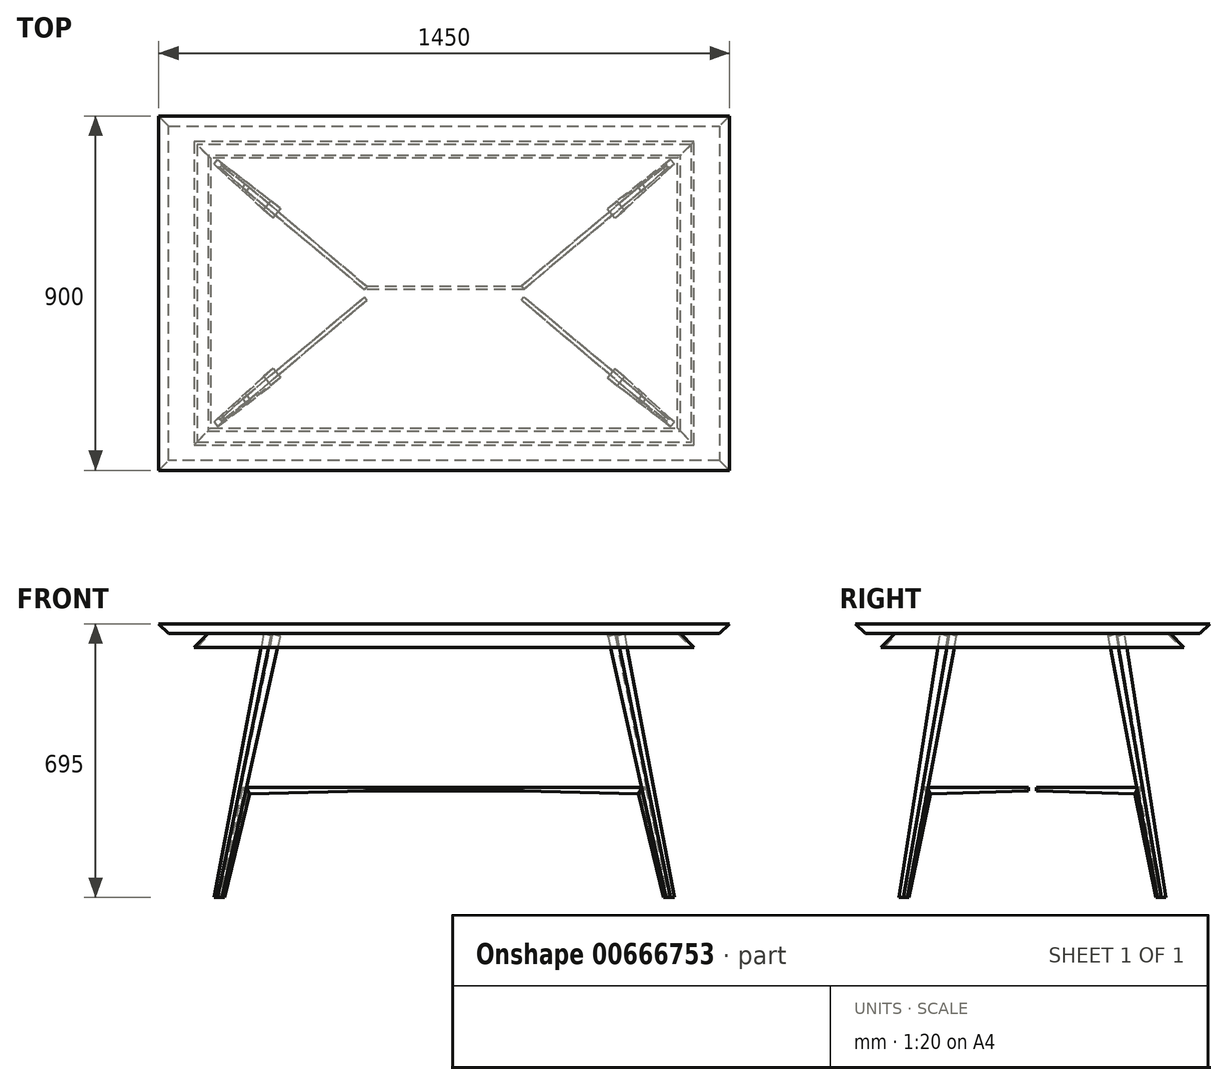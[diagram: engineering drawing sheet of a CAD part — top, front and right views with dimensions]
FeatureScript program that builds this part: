
annotation { "Feature Type Name" : "Feature", "Feature Type Description" : "" }
export const myFeature = defineFeature(function(context is Context, id is Id, definition is map)
    precondition{}
    {
        {
            assignVariable(context, id + "F0", {"name" : "t_l", "anyValue" : 30});
        }
        {
            var Q0;
            Q0=qCreatedBy(makeId("Top.planeOp"),FACE);
            var sketch = newSketch(context, id + "F1", { "sketchPlane" : qUnion([Q0])});
            skLineSegment(sketch, "E0.bottom", {"start": v(600, -350) * mm, "end": v(-600, -350) * mm});
            skLineSegment(sketch, "E0.top", {"start": v(600, 350) * mm, "end": v(-600, 350) * mm});
            skLineSegment(sketch, "E0.left", {"start": v(600, -350) * mm, "end": v(600, 350) * mm});
            skLineSegment(sketch, "E0.right", {"start": v(-600, -350) * mm, "end": v(-600, 350) * mm});
            skPoint(sketch, "E0.middle", {"position": v(0, 0) * mm});
            skLineSegment(sketch, "E1", {"start": v(-600, -350) * mm, "end": v(-182.89, 0) * mm});
            skLineSegment(sketch, "E2", {"start": v(-600, 0) * mm, "end": v(600, 0) * mm});
            skSolve(sketch);
        }
        {
            var Q0;
            Q0=sQuery(id+"F1.wireOp",EDGE,"E1");
            cPlane(context, id + "F2", {"entities" : qUnion([Q0]), "cplaneType" : CPlaneType.LINE_ANGLE, "offset" : 25 * mm, "angle" : 0 * degree, "width" : 150 * mm, "height" : 150 * mm});
        }
        {
            var Q0;
            Q0=qCreatedBy(id+"F2.planeOp",FACE);
            var sketch = newSketch(context, id + "F3", { "sketchPlane" : qUnion([Q0])});
            skLineSegment(sketch, "E3", {"start": v(0, 0) * mm, "end": v(0, -670) * mm, "construction": true});
            skLineSegment(sketch, "E4", {"start": v(486.97, 0) * mm, "end": v(658.66, -670) * mm});
            skLineSegment(sketch, "E5", {"start": v(658.66, -670) * mm, "end": v(643.18, -670) * mm});
            skLineSegment(sketch, "E6", {"start": v(643.18, -670) * mm, "end": v(455.82, 0) * mm});
            skLineSegment(sketch, "E7", {"start": v(455.82, 0) * mm, "end": v(486.97, 0) * mm});
            skLineSegment(sketch, "E8", {"start": v(643.18, -670) * mm, "end": v(631.18, -670) * mm});
            skLineSegment(sketch, "E9", {"start": v(631.18, -670) * mm, "end": v(551.03, -407.1) * mm});
            skLineSegment(sketch, "E10", {"start": v(551.03, -407.1) * mm, "end": v(161.6, -399.33) * mm, "construction": true});
            skLineSegment(sketch, "E11", {"start": v(161.6, -399.33) * mm, "end": v(161.6, -390) * mm});
            skLineSegment(sketch, "E12", {"start": v(161.6, -390) * mm, "end": v(564.88, -390) * mm, "construction": true});
            skLineSegment(sketch, "E13", {"start": v(471.4, 0) * mm, "end": v(650.92, -670) * mm, "construction": true});
            skLineSegment(sketch, "E14", {"start": v(486.97, 0) * mm, "end": v(458, -7.76) * mm, "construction": true});
            skLineSegment(sketch, "E15", {"start": v(643.18, -670) * mm, "end": v(657.67, -666.12) * mm, "construction": true});
            skLineSegment(sketch, "E16", {"start": v(551.03, -407.1) * mm, "end": v(564.88, -390) * mm});
            skPoint(sketch, "E17", {"position": v(140.1, 0) * mm});
            skLineSegment(sketch, "E18", {"start": v(140.1, 0) * mm, "end": v(140.1, -670) * mm, "construction": true});
            skLineSegment(sketch, "E19", {"start": v(650.92, -670) * mm, "end": v(140.1, -670) * mm, "construction": true});
            skSolve(sketch);
        }
        {
            var Q0;
            Q0=makeQuery(id+"F3.imprint","IMPRINT",FACE,{"disambiguationData":[TD([[makeQuery(id+"F3.imprint","IMPRINT",EDGE,{"derivedFrom":sQuery(id+"F3.wireOp",EDGE,"E4")}),-1.0]])]});
            extrude(context, id + "F4", {"entities" : qUnion([Q0]), "endBound" : BoundingType.SYMMETRIC, "depth" : (getVariable(context, 't_l')) * mm, "offsetDistance" : 25 * mm});
        }
        {
            var Q0;
            Q0=makeQuery(id+"F4.opExtrude","SWEPT_FACE",FACE,{"disambiguationData":[OSD([sQuery(id+"F3.wireOp",EDGE,"E4")])]});
            var sketch = newSketch(context, id + "F5", { "sketchPlane" : qUnion([Q0])});
            skLineSegment(sketch, "E20.0", {"start": v(-105.12, -145.38) * mm, "end": v(-75.75, -139.26) * mm});
            skPoint(sketch, "E21.0", {"position": v(50.6, -819.43) * mm});
            skLineSegment(sketch, "E22", {"start": v(43.26, -820.96) * mm, "end": v(57.95, -817.9) * mm});
            skLineSegment(sketch, "E23.0", {"start": v(35.92, -822.5) * mm, "end": v(65.29, -816.37) * mm});
            skLineSegment(sketch, "E24.0", {"start": v(-75.75, -139.26) * mm, "end": v(65.29, -816.37) * mm});
            skLineSegment(sketch, "E25.0", {"start": v(-105.12, -145.38) * mm, "end": v(35.92, -822.5) * mm});
            skLineSegment(sketch, "E26", {"start": v(57.95, -817.9) * mm, "end": v(-75.75, -139.26) * mm});
            skLineSegment(sketch, "E27", {"start": v(-105.12, -145.38) * mm, "end": v(43.26, -820.96) * mm});
            skSolve(sketch);
        }
        {
            var Q0;
            {var subQ0=sQuery(id+"F5.wireOp",EDGE,"E25.0");Q0=makeQuery(id+"F5.imprint","IMPRINT",FACE,{"disambiguationData":[TD([[makeQuery(id+"F5.imprint","IMPRINT",EDGE,{"derivedFrom":subQ0}),1.0]])]});}
            var Q1;
            {var subQ0=sQuery(id+"F5.wireOp",EDGE,"E24.0");Q1=makeQuery(id+"F5.imprint","IMPRINT",FACE,{"disambiguationData":[TD([[makeQuery(id+"F5.imprint","IMPRINT",EDGE,{"derivedFrom":subQ0}),-1.0]])]});}
            extrude(context, id + "F6", {"entities" : qUnion([Q0, Q1]), "operationType" : NewBodyOperationType.REMOVE, "endBound" : BoundingType.THROUGH_ALL, "oppositeDirection" : true, "depth" : 25 * mm, "offsetDistance" : 25 * mm});
        }
        {
            var Q0;
            {var subQ0=sQuery(id+"F3.wireOp",EDGE,"E8");Q0=makeQuery(id+"F3.imprint","IMPRINT",FACE,{"disambiguationData":[TD([[makeQuery(id+"F3.imprint","IMPRINT",EDGE,{"derivedFrom":subQ0}),-1.0]])]});}
            extrude(context, id + "F7", {"entities" : qUnion([Q0]), "endBound" : BoundingType.SYMMETRIC, "depth" : 12 * mm, "offsetDistance" : 25 * mm});
        }
        {
            var Q0;
            Q0=makeQuery(id+"F4.opExtrude","SWEPT_FACE",FACE,{"disambiguationData":[OSD([sQuery(id+"F3.wireOp",EDGE,"E6")])]});
            var sketch = newSketch(context, id + "F8", { "sketchPlane" : qUnion([Q0])});
            skLineSegment(sketch, "E28.0", {"start": v(-71.6, -822.92) * mm, "end": v(-7.5, -539.33) * mm});
            skLineSegment(sketch, "E29.0", {"start": v(4.2, -541.97) * mm, "end": v(-7.5, -539.33) * mm});
            skLineSegment(sketch, "E30.0", {"start": v(-59.89, -825.56) * mm, "end": v(4.2, -541.97) * mm});
            skLineSegment(sketch, "E31.0", {"start": v(-59.89, -825.56) * mm, "end": v(-71.6, -822.92) * mm});
            skLineSegment(sketch, "E32", {"start": v(4.2, -541.97) * mm, "end": v(-62.96, -824.87) * mm});
            skLineSegment(sketch, "E33", {"start": v(-68.52, -823.61) * mm, "end": v(-7.5, -539.33) * mm});
            skSolve(sketch);
        }
        {
            var Q0;
            {var subQ0=sQuery(id+"F8.wireOp",EDGE,"E30.0");Q0=makeQuery(id+"F8.imprint","IMPRINT",FACE,{"disambiguationData":[TD([[makeQuery(id+"F8.imprint","IMPRINT",EDGE,{"derivedFrom":subQ0}),1.0]])]});}
            var Q1;
            {var subQ0=sQuery(id+"F8.wireOp",EDGE,"E28.0");Q1=makeQuery(id+"F8.imprint","IMPRINT",FACE,{"disambiguationData":[TD([[makeQuery(id+"F8.imprint","IMPRINT",EDGE,{"derivedFrom":subQ0}),-1.0]])]});}
            var Q2;
            Q2=makeQuery(id+"F7.opExtrude","SWEPT_FACE",FACE,{"disambiguationData":[OSD([sQuery(id+"F3.wireOp",EDGE,"E9")])]});
            extrude(context, id + "F9", {"entities" : qUnion([Q0, Q1]), "operationType" : NewBodyOperationType.REMOVE, "endBound" : BoundingType.UP_TO_SURFACE, "depth" : 25 * mm, "endBoundEntityFace" : qUnion([Q2]), "offsetDistance" : 25 * mm});
        }
        {
            var Q0;
            Q0=sQuery(id+"F3.wireOp",EDGE,"E12");
            var Q1;
            Q1=sQuery(id+"F3.wireOp",EDGE,"E10");
            var Q2;
            Q2=sQuery(id+"F3.wireOp",EDGE,"E11");
            extrude(context, id + "F10", {"bodyType" : ToolBodyType.SURFACE, "surfaceEntities" : qUnion([Q0, Q1, Q2]), "endBound" : BoundingType.SYMMETRIC, "depth" : 10 * mm, "offsetDistance" : 25 * mm});
        }
        {
            var Q1;
            Q1=makeQuery(id+"F7.opExtrude","SWEPT_FACE",FACE,{"disambiguationData":[OSD([sQuery(id+"F3.wireOp",EDGE,"E16")])]});
            var Q2;
            Q2=makeQuery(id+"F10.opExtrude","SWEPT_FACE",FACE,{"disambiguationData":[OSD([sQuery(id+"F3.wireOp",EDGE,"E11")])]});
            loft(context, id + "F11", {"operationType" : NewBodyOperationType.ADD, "sheetProfilesArray" : [{ "sheetProfileEntities" : qUnion([Q1]) }, { "sheetProfileEntities" : qUnion([Q2]) }]});
        }
        {
            var Q0;
            {var subQ0=sQuery(id+"F1.wireOp",EDGE,"E0.bottom");Q0=makeQuery(id+"F1.imprint","IMPRINT",FACE,{"disambiguationData":[TD([[makeQuery(id+"F1.imprint","IMPRINT",EDGE,{"derivedFrom":subQ0}),-1.0]])]});}
            var sketch = newSketch(context, id + "F12", { "sketchPlane" : qUnion([Q0])});
            skPoint(sketch, "E34.0", {"position": v(-434.38, -191.45) * mm});
            skPoint(sketch, "E35.0", {"position": v(-438.96, -234.45) * mm});
            skLineSegment(sketch, "E36", {"start": v(-438.96, -234.45) * mm, "end": v(-434.38, -191.45) * mm, "construction": true});
            skLineSegment(sketch, "E37.0", {"start": v(-434.38, -191.45) * mm, "end": v(-415.1, -214.43) * mm});
            skLineSegment(sketch, "E38.0", {"start": v(-415.1, -214.43) * mm, "end": v(-438.96, -234.45) * mm});
            skLineSegment(sketch, "E39", {"start": v(-434.38, -191.45) * mm, "end": v(-434.38, -230.61) * mm});
            skSolve(sketch);
        }
        {
            var Q0;
            Q0=makeQuery(id+"F4.opExtrude","SWEPT_BODY",BODY,{"disambiguationData":[OSD([sQuery(id+"F3.wireOp",EDGE,"E4"),sQuery(id+"F3.wireOp",EDGE,"E5"),sQuery(id+"F3.wireOp",EDGE,"E6"),sQuery(id+"F3.wireOp",EDGE,"E7")])]});
            var Q1;
            Q1=makeQuery(id+"F7.opExtrude","SWEPT_BODY",BODY,{"disambiguationData":[OSD([sQuery(id+"F3.wireOp",EDGE,"E6"),sQuery(id+"F3.wireOp",EDGE,"E8"),sQuery(id+"F3.wireOp",EDGE,"E9"),sQuery(id+"F3.wireOp",EDGE,"E16")])]});
            var Q2;
            Q2=qCreatedBy(makeId("Front.planeOp"),FACE);
            mirror(context, id + "F13", {"operationType" : NewBodyOperationType.ADD, "entities" : qUnion([Q0, Q1]), "mirrorPlane" : qUnion([Q2])});
        }
        {
            var Q0;
            Q0=makeQuery(id+"F4.opExtrude","SWEPT_BODY",BODY,{"disambiguationData":[OSD([sQuery(id+"F3.wireOp",EDGE,"E4"),sQuery(id+"F3.wireOp",EDGE,"E5"),sQuery(id+"F3.wireOp",EDGE,"E6"),sQuery(id+"F3.wireOp",EDGE,"E7")])]});
            var Q1;
            Q1=makeQuery(id+"F7.opExtrude","SWEPT_BODY",BODY,{"disambiguationData":[OSD([sQuery(id+"F3.wireOp",EDGE,"E6"),sQuery(id+"F3.wireOp",EDGE,"E8"),sQuery(id+"F3.wireOp",EDGE,"E9"),sQuery(id+"F3.wireOp",EDGE,"E16")])]});
            var Q2;
            Q2=makeQuery(id+"F13.opPattern","COPY",BODY,{"derivedFrom":makeQuery(id+"F4.opExtrude","SWEPT_BODY",BODY,{"disambiguationData":[OSD([sQuery(id+"F3.wireOp",EDGE,"E4"),sQuery(id+"F3.wireOp",EDGE,"E5"),sQuery(id+"F3.wireOp",EDGE,"E6"),sQuery(id+"F3.wireOp",EDGE,"E7")])]}),"instanceName":"1"});
            var Q3;
            Q3=qCreatedBy(makeId("Right.planeOp"),FACE);
            mirror(context, id + "F14", {"entities" : qUnion([Q0, Q1, Q2]), "mirrorPlane" : qUnion([Q3])});
        }
        {
            var Q0;
            Q0=makeQuery(id+"F13.opPattern","COPY",FACE,{"derivedFrom":makeQuery(id+"F11.opLoft","SWEPT_FACE",FACE,{"disambiguationData":[OSD([sQuery(id+"F3.wireOp",VERTEX,"E11.end"),sQuery(id+"F3.wireOp",EDGE,"E6"),sQuery(id+"F3.wireOp",EDGE,"E16"),sQuery(id+"F8.wireOp",EDGE,"E28.0"),sQuery(id+"F8.wireOp",EDGE,"E29.0"),sQuery(id+"F8.wireOp",EDGE,"E30.0"),sQuery(id+"F8.wireOp",EDGE,"E32"),sQuery(id+"F8.wireOp",EDGE,"E33")])]}),"instanceName":"1"});
            var sketch = newSketch(context, id + "F15", { "sketchPlane" : qUnion([Q0])});
            skLineSegment(sketch, "E40.0", {"start": v(-202.57, 10) * mm, "end": v(-196.14, 17.65) * mm});
            skLineSegment(sketch, "E41.0", {"start": v(202.57, 10) * mm, "end": v(196.14, 17.65) * mm});
            skLineSegment(sketch, "E42", {"start": v(202.57, 10) * mm, "end": v(-202.57, 10) * mm});
            skLineSegment(sketch, "E43", {"start": v(-196.14, 17.65) * mm, "end": v(196.14, 17.65) * mm});
            skSolve(sketch);
        }
        {
            var Q0;
            Q0=makeQuery(id+"F15.imprint","IMPRINT",FACE,{"disambiguationData":[TD([[makeQuery(id+"F15.imprint","IMPRINT",EDGE,{"derivedFrom":sQuery(id+"F15.wireOp",EDGE,"E40.0")}),-1.0]])]});
            var Q1;
            {var subQ0=sQuery(id+"F3.wireOp",VERTEX,"E11.start");Q1=makeQuery(id+"F13.opPattern","COPY",VERTEX,{"derivedFrom":makeQuery(id+"F11.opLoft","MID_CAP_VERTEX",VERTEX,{"disambiguationData":[OSD([subQ0]),TDD([makeQuery(id+"F10.opExtrude","CAP_VERTEX",VERTEX,{"disambiguationData":[OSD([subQ0])],"isStart":false})])],"capPos":1.0}),"instanceName":"1"});}
            extrude(context, id + "F16", {"entities" : qUnion([Q0]), "operationType" : NewBodyOperationType.ADD, "endBound" : BoundingType.UP_TO_VERTEX, "oppositeDirection" : true, "depth" : 25 * mm, "endBoundEntityVertex" : qUnion([Q1]), "offsetDistance" : 25 * mm});
        }
        {
            var Q0;
            {var subQ0=sQuery(id+"F1.wireOp",EDGE,"E0.bottom");Q0=makeQuery(id+"F1.imprint","IMPRINT",FACE,{"disambiguationData":[TD([[makeQuery(id+"F1.imprint","IMPRINT",EDGE,{"derivedFrom":subQ0}),-1.0]])]});}
            var Q1;
            {var subQ0=sQuery(id+"F1.wireOp",EDGE,"E1");Q1=makeQuery(id+"F1.imprint","IMPRINT",FACE,{"disambiguationData":[TD([[makeQuery(id+"F1.imprint","IMPRINT",EDGE,{"derivedFrom":subQ0}),1.0]])]});}
            var Q2;
            {var subQ4=sQuery(id+"F1.wireOp",EDGE,"E0.top");Q2=makeQuery(id+"F1.imprint","IMPRINT",FACE,{"disambiguationData":[TD([[makeQuery(id+"F1.imprint","IMPRINT",EDGE,{"derivedFrom":subQ4}),1.0]])]});}
            extrude(context, id + "F17", {"entities" : qUnion([Q0, Q1, Q2]), "oppositeDirection" : true, "depth" : 35 * mm, "offsetDistance" : 25 * mm, "hasDraft" : true, "draftAngle" : 45 * degree});
        }
        {
            var Q0;
            {var subQ0=sQuery(id+"F1.wireOp",EDGE,"E0.bottom");Q0=makeQuery(id+"F1.imprint","IMPRINT",FACE,{"disambiguationData":[TD([[makeQuery(id+"F1.imprint","IMPRINT",EDGE,{"derivedFrom":subQ0}),-1.0]])]});}
            var sketch = newSketch(context, id + "F18", { "sketchPlane" : qUnion([Q0])});
            skLineSegment(sketch, "E44.bottom", {"start": v(700, -425) * mm, "end": v(-700, -425) * mm});
            skLineSegment(sketch, "E44.top", {"start": v(700, 425) * mm, "end": v(-700, 425) * mm});
            skLineSegment(sketch, "E44.left", {"start": v(700, -425) * mm, "end": v(700, 425) * mm});
            skLineSegment(sketch, "E44.right", {"start": v(-700, -425) * mm, "end": v(-700, 425) * mm});
            skPoint(sketch, "E44.middle", {"position": v(0, 0) * mm});
            skSolve(sketch);
        }
        {
            var Q0;
            Q0=makeQuery(id+"F18.imprint","IMPRINT",FACE,{"disambiguationData":[TD([[makeQuery(id+"F18.imprint","IMPRINT",EDGE,{"derivedFrom":sQuery(id+"F18.wireOp",EDGE,"E44.bottom")}),-1.0]])]});
            var Q1;
            {var subQ0=sQuery(id+"F1.wireOp",EDGE,"E0.bottom");Q1=makeQuery(id+"F18.imprint","IMPRINT",FACE,{"disambiguationData":[TD([[makeQuery(id+"F18.imprint","IMPRINT",EDGE,{"derivedFrom":makeQuery(id+"F1.imprint","IMPRINT",EDGE,{"derivedFrom":subQ0})}),-1.0]])]});}
            extrude(context, id + "F19", {"entities" : qUnion([Q0, Q1]), "depth" : 25 * mm, "offsetDistance" : 25 * mm, "hasDraft" : true, "draftAngle" : 45 * degree});
        }
        {
            var Q0;
            Q0=makeQuery(id+"F17.opExtrude","CAP_FACE",FACE,{"disambiguationData":[OSD([sQuery(id+"F1.wireOp",EDGE,"E0.bottom"),sQuery(id+"F1.wireOp",EDGE,"E0.top"),sQuery(id+"F1.wireOp",EDGE,"E0.left"),sQuery(id+"F1.wireOp",EDGE,"E0.right")])],"isStart":true});
            var Q1;
            Q1=makeQuery(id+"F17.opExtrude","CAP_FACE",FACE,{"disambiguationData":[OSD([sQuery(id+"F1.wireOp",EDGE,"E0.bottom"),sQuery(id+"F1.wireOp",EDGE,"E0.top"),sQuery(id+"F1.wireOp",EDGE,"E0.left"),sQuery(id+"F1.wireOp",EDGE,"E0.right")])],"isStart":false});
            shell(context, id + "F20", {"entities" : qUnion([Q0, Q1]), "thickness" : 5 * mm});
        }
    });
